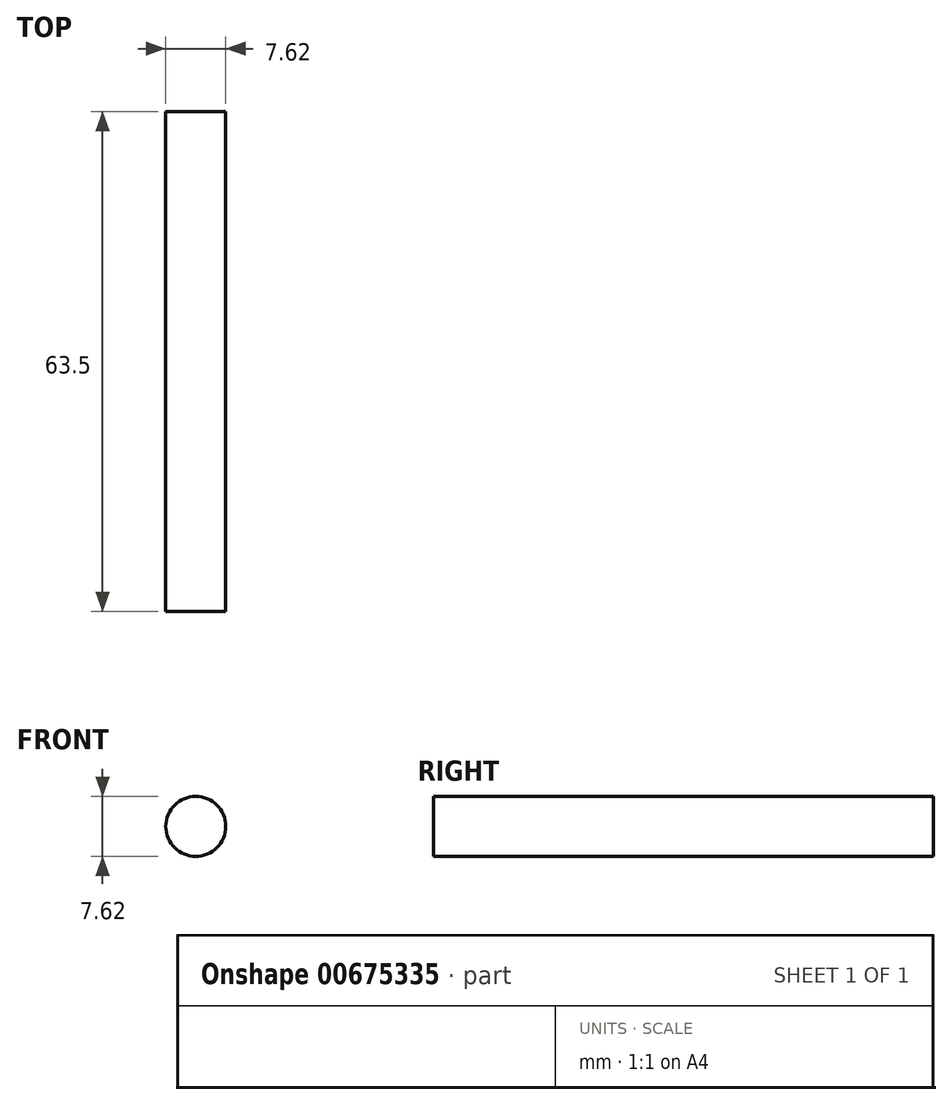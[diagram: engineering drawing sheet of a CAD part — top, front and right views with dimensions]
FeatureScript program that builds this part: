
annotation { "Feature Type Name" : "Feature", "Feature Type Description" : "" }
export const myFeature = defineFeature(function(context is Context, id is Id, definition is map)
    precondition{}
    {
        {
            var Q0;
            Q0=qCreatedBy(makeId("Front.planeOp"),FACE);
            var sketch = newSketch(context, id + "F0", { "sketchPlane" : qUnion([Q0])});
            skCircle(sketch, "E0", {"center": v(15.5, 0) * mm, "radius": 3.81 * mm});
            skSolve(sketch);
        }
        {
            var Q0;
            Q0 = qSketchRegion(id + "F0", true);
            extrude(context, id + "F1", {"entities" : qUnion([Q0]), "oppositeDirection" : true, "depth" : 63.5 * mm, "offsetDistance" : 25.4 * mm});
        }
    });
